# Revit family: xxxFaucet-Lavatory-Grohe-Essence_New-23538_Series
name_source: partatom
category: Plumbing Fixtures
units: mm (PartAtom-declared; Revit-internal decimal feet)

## family parameters
Always vertical = No
Cut with Voids When Loaded = No
OmniClass Number = 23.45.55.14
OmniClass Title = Single Faucets
Part Type = Normal
Room Calculation Point = No
Round Connector Dimension = Use Diameter
Shared = Yes
Work Plane-Based = Yes

## types (5) — shared parameters
ADA Compliant = Yes
Assembly Code = D2020300
CW Connection = No
CWFU = 1.5
Compliance Certifications = Energy Policy Act of 1992, NSF 61, ASME A112.18.1/CSA B125.1, US Federal and State material regulations, EPA WaterSense®, ICC/ANSI A117.1, CalGreen & LOGO NSF
Default Elevation = 0"
Description = Single Hole Single-Handle Deck Mount Vessel Sink Faucet 1.2 GPM
Flow Rate = 1.2 gpm (4.5 L/min)
HW Connection = No
HWFU = 1.5
Height = 14 5/16"
Height- Spout = 12 11/16"
Installation Instruction Link = https://americanstandard.box.com
Installation Type = Deck-Mounted
Length = 7 1/16"
Manufacturer = Grohe
Max. Hot Water Temp. = 158 °F
Min Max. Operating Pressure = 7.25 psi to 145 psi
Price = Prices may vary. Please consult Manufacturer Representative for most up-to-date price list.
Product Documentation Link = https://americanstandard.box.com
Product Page URL = https://www.grohe.us
Revised Date = 03/02/2022
Tempered Water Connection = Yes
Tempered Water Connection Diameter = 3/8"
URL = https://www.grohe.us
Vent Connection = No
WFU = 2
Warranty Information = Limited Lifetime Warranty
Waste Connection = No
cUPC Compliant = Yes

## per-type parameters (varying)
| type | Finish | Material |
| 2353800A | Brass-Grohe-00A-StarLight Chrome | Brass-Grohe-00A-StarLight Chrome |
| 23538BEA | Brass-Grohe-BEA-Polished Nickel Infinity Finish | Brass-Grohe-BEA-Polished Nickel Infinity Finish |
| 23538GNA | Brass-Grohe-GNA-Brushed Cool Sunrise | Brass-Grohe-GNA-Brushed Cool Sunrise |
| 23538A0A | Brass-Grohe-A0A-Hard Graphite | Brass-Grohe-A0A-Hard Graphite |
| 23538ENA | Brass-Grohe-ENA-Brushed Nickel Infinity Finish | Brass-Grohe-ENA-Brushed Nickel Infinity Finish |

note: column(s) folded — value = type name in every type: Model

## geometry (parser evidence)
native form markers: Sweep x1
no freeform markers — native parametric forms only
